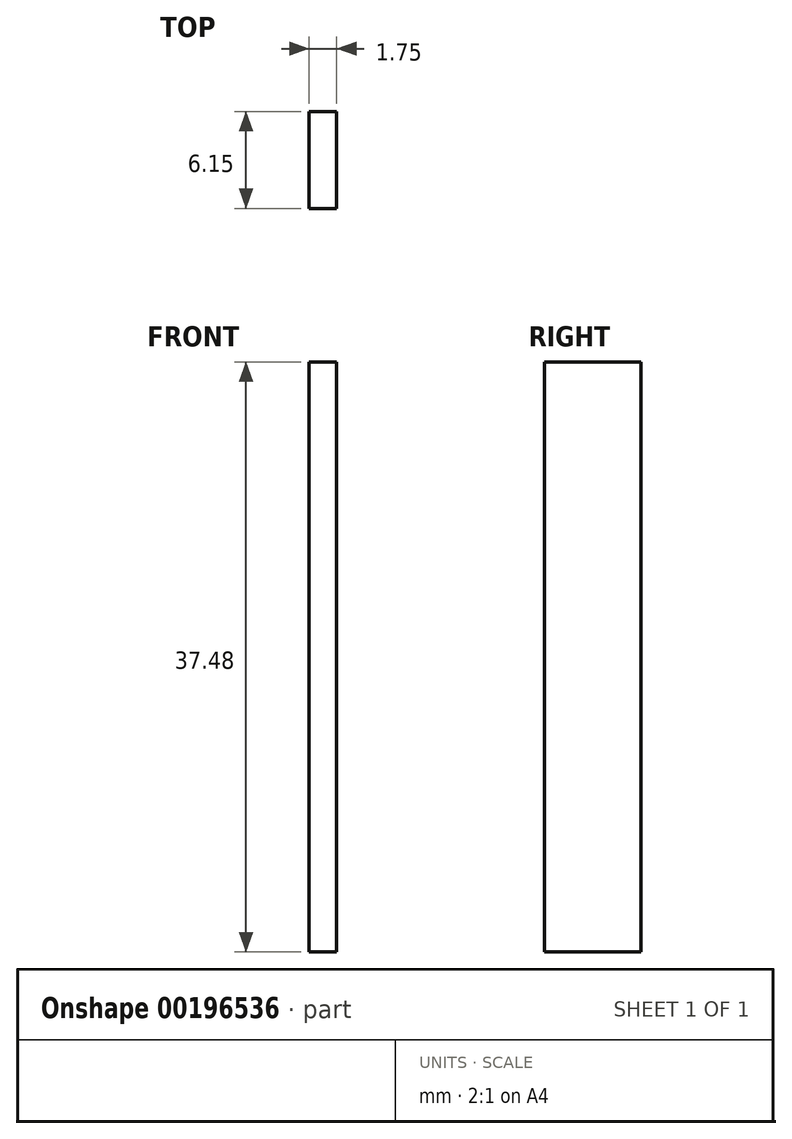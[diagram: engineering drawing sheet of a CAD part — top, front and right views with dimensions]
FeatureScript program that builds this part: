
annotation { "Feature Type Name" : "Feature", "Feature Type Description" : "" }
export const myFeature = defineFeature(function(context is Context, id is Id, definition is map)
    precondition{}
    {
        {
            var Q0;
            Q0=qCreatedBy(makeId("Front.planeOp"),FACE);
            var sketch = newSketch(context, id + "F0", { "sketchPlane" : qUnion([Q0])});
            skLineSegment(sketch, "E0.bottom", {"start": v(0, 0) * mm, "end": v(-1.75, 0) * mm});
            skLineSegment(sketch, "E0.top", {"start": v(0, 37.48) * mm, "end": v(-1.75, 37.48) * mm});
            skLineSegment(sketch, "E0.left", {"start": v(0, 0) * mm, "end": v(0, 37.48) * mm});
            skLineSegment(sketch, "E0.right", {"start": v(-1.75, 0) * mm, "end": v(-1.75, 37.48) * mm});
            skSolve(sketch);
        }
        {
            var Q0;
            Q0=makeQuery(id+"F0.imprint","IMPRINT",FACE,{"disambiguationData":[TD([[makeQuery(id+"F0.imprint","IMPRINT",EDGE,{"derivedFrom":sQuery(id+"F0.wireOp",EDGE,"E0.bottom")}),-1.0]])]});
            extrude(context, id + "F1", {"entities" : qUnion([Q0]), "depth" : 6.15 * mm});
        }
    });
